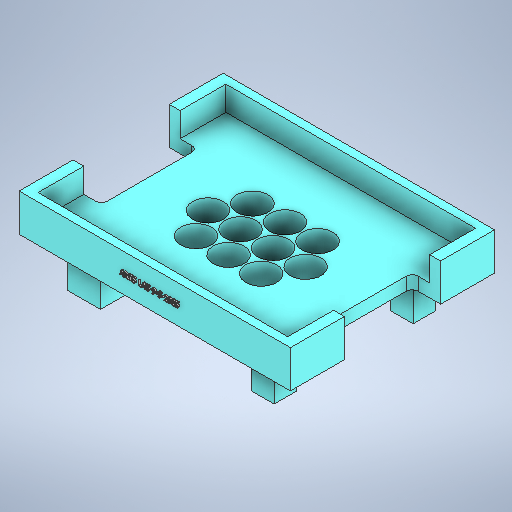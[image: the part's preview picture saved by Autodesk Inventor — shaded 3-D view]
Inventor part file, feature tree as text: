
AUTODESK INVENTOR PART (.ipt)
format: ipt  version: 2025.2 (Build 292293000, 293)  size: 1,257,984 bytes
history: native  units: mm
features: projected_geometry x10, extrude x9, sketch x9
ambient origin geometry x8: Origin, YZ Plane, XZ Plane, XY Plane, X Axis, Y Axis, Z Axis, Center Point
bodies: Solid1 (feature_tree)
feature tree (28):
  extrude  "Extrusion1"  Depth=19.0mm
  sketch  "Sketch4"  dims[d4=19.0mm d6=19.0mm]
  extrude  "Extrusion7"  Depth=19.0mm
  sketch  "Sketch5"  dims[d8=19.0mm d10=19.0mm]
  extrude  "Extrusion8"  Depth=19.0mm
  extrude  "Extrusion6"  Depth=19.0mm
  extrude  "Extrusion9"  Depth=15.0mm TaperAngle=0.0deg
  extrude  "Extrusion11"  Depth=1.0mm
  extrude  "Extrusion12"  Depth=7.23mm
  extrude  "Extrusion14"  Depth=7.23mm
  extrude  "Extrusion15"  TaperAngle=0.0deg  [1 undecoded]
  sketch  "Sketch1"  dims[d0=19.0mm d2=19.0mm]
  projected_geometry  "Projected Loop1"
  sketch  "Sketch6"  dims[d11=19.0mm d13=19.0mm]
  projected_geometry  "Projected Loop4"
  sketch  "Sketch7"  dims[d14=19.0mm]
  projected_geometry  "Projected Loop5"
  projected_geometry  "Projected Loop6"
  sketch  "Sketch10"  dims[d16=20.0mm d17=20.0mm d18=20.0mm d19=20.0mm d20=20.0mm d21=20.0mm d22=20.0mm d23=20.0mm d24=15.0mm d25=0.0mm]
  projected_geometry  "Projected Loop9"
  sketch  "Sketch11"  dims[d53=19.0mm d91=1.0mm]
  projected_geometry  "Projected Loop10"
  projected_geometry  "Projected Loop11"
  sketch  "Sketch13"  dims[d104=153.4mm d123=7.23mm]
  projected_geometry  "Projected Loop13"
  projected_geometry  "Projected Loop14"
  sketch  "Sketch14"  dims[d124=7.23mm d125=7.23mm d126=0.0mm d127=0.0mm d140=7.23mm d144=21.0mm d145=21.0mm d146=21.0mm d147=21.0mm d148=21.0mm d149=21.0mm d150=21.0mm d151=21.0mm d152=21.0mm d153=21.0mm d154=23.0mm d155=23.0mm d156=23.0mm d157=23.0mm d158=23.0mm d159=23.0mm d160=23.0mm d161=23.0mm d162=23.0mm d163=23.0mm d164=115.4mm d165=8.0mm d166=0.0mm d169=5.0mm d170=6.646447mm d171=166.692894mm d172=125.4mm d173=15.0mm d174=8.0mm d175=0.0mm d176=0.0mm d177=0.0mm d178=0.0mm d179=31.75mm d180=7.228mm d181=7.228mm d182=31.75mm d183=31.75mm d184=7.228mm d185=7.228mm d186=31.75mm d209=30.0mm d210=20.0mm d211=20.0mm d212=20.0mm d213=15.0mm d214=15.0mm d215=30.0mm d216=20.0mm d217=14.0mm d218=14.0mm d219=25.0mm d220=0.0mm d221=6.646447mm d222=70.0mm d223=0.0mm d224=30.0mm d225=30.0mm d226=20.0mm d227=20.0mm d231=10.0mm d232=0.0mm d233=76.7mm d234=76.7mm d235=17.489447mm d236=17.489447mm d237=1.0mm d238=0.0mm d228=0.5mm d229=0.872665mm d230=0.5mm]
  projected_geometry  "Projected Loop15"
note: 1 required parameter value undecoded (feature->parameter linkage not recoverable at this tier; creation-order binding heuristic only, values carry confidence <= 0.55)
